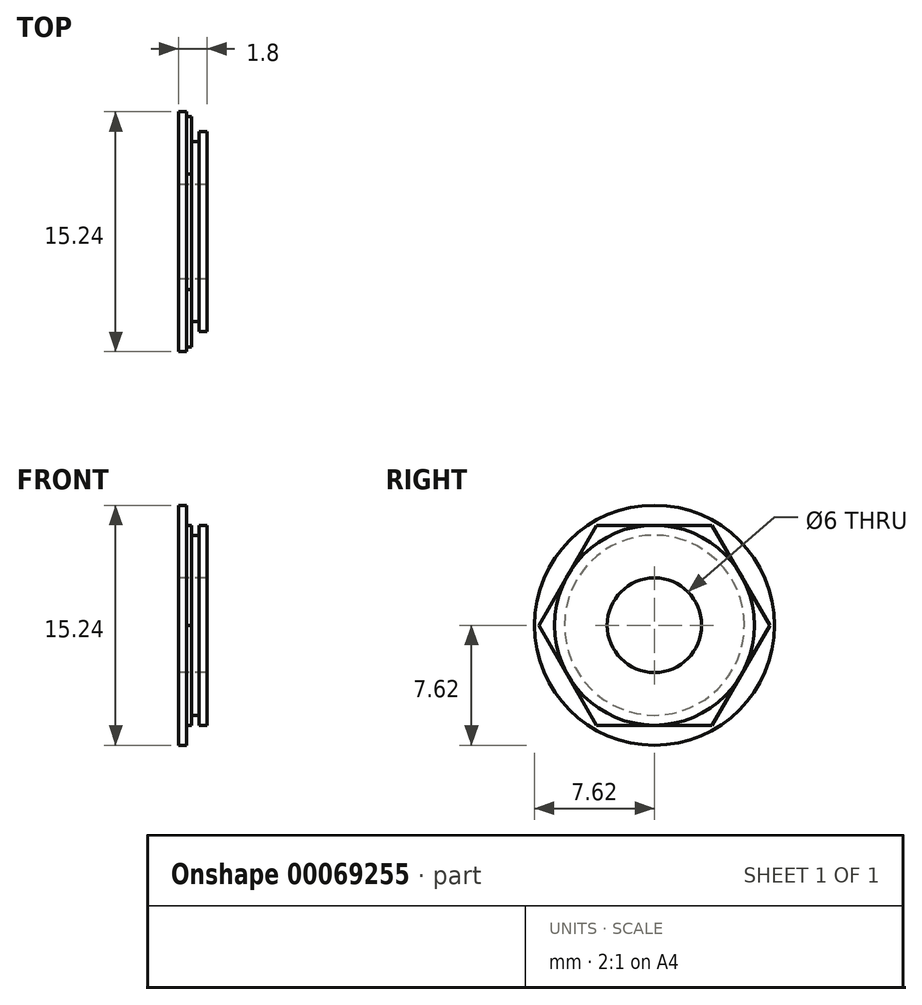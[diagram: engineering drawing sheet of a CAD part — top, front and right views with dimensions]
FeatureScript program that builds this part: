
annotation { "Feature Type Name" : "Feature", "Feature Type Description" : "" }
export const myFeature = defineFeature(function(context is Context, id is Id, definition is map)
    precondition{}
    {
        {
            assignVariable(context, id + "F0", {"name" : "shoulder_length", "anyValue" : .5});
        }
        {
            assignVariable(context, id + "F1", {"name" : "hex_length", "anyValue" : 0.3});
        }
        {
            var Q0;
            Q0=qCreatedBy(makeId("Right.planeOp"),FACE);
            var sketch = newSketch(context, id + "F2", { "sketchPlane" : qUnion([Q0])});
            skCircle(sketch, "E0", {"center": v(0, 0) * mm, "radius": 7.62 * mm});
            skCircle(sketch, "E1.cCircle", {"center": v(0, 0) * mm, "radius": 6.35 * mm});
            skLineSegment(sketch, "E1.0", {"start": v(-3.67, 6.35) * mm, "end": v(3.67, 6.35) * mm});
            skLineSegment(sketch, "E1.1", {"start": v(3.67, 6.35) * mm, "end": v(7.33, 0) * mm});
            skLineSegment(sketch, "E1.2", {"start": v(7.33, 0) * mm, "end": v(3.67, -6.35) * mm});
            skLineSegment(sketch, "E1.3", {"start": v(3.67, -6.35) * mm, "end": v(-3.67, -6.35) * mm});
            skLineSegment(sketch, "E1.4", {"start": v(-3.67, -6.35) * mm, "end": v(-7.33, 0) * mm});
            skLineSegment(sketch, "E1.5", {"start": v(-7.33, 0) * mm, "end": v(-3.67, 6.35) * mm});
            skPoint(sketch, "E1.0.midPoint", {"position": v(0, 6.35) * mm});
            skCircle(sketch, "E2.0", {"center": v(0, 0) * mm, "radius": 5.72 * mm});
            skCircle(sketch, "E3", {"center": v(0, 0) * mm, "radius": 3 * mm});
            skSolve(sketch);
        }
        {
            var Q0;
            Q0=makeQuery(id+"F2.imprint","IMPRINT",FACE,{"disambiguationData":[TD([[makeQuery(id+"F2.imprint","IMPRINT",EDGE,{"derivedFrom":sQuery(id+"F2.wireOp",EDGE,"E0")}),1.0]])]});
            extrude(context, id + "F3", {"entities" : qUnion([Q0]), "depth" : (getVariable(context, 'shoulder_length')) * mm});
        }
        {
            var Q0;
            {var subQ0=sQuery(id+"F2.wireOp",EDGE,"E1.0");var subQ1=sQuery(id+"F2.wireOp",EDGE,"E1.cCircle");var subQ2=makeQuery(id+"F2.imprint","INTERSECT",VERTEX,{"derivedFrom":[subQ1,subQ0]});Q0=makeQuery(id+"F2.imprint","IMPRINT",FACE,{"disambiguationData":[TD([[makeQuery(id+"F2.imprint","IMPRINT",EDGE,{"disambiguationData":[TD([[subQ2,-1.0]])],"derivedFrom":subQ1}),-1.0]])]});}
            var Q1;
            {var subQ0=sQuery(id+"F2.wireOp",EDGE,"E1.0");var subQ1=sQuery(id+"F2.wireOp",EDGE,"E1.cCircle");var subQ2=makeQuery(id+"F2.imprint","INTERSECT",VERTEX,{"derivedFrom":[subQ1,subQ0]});Q1=makeQuery(id+"F2.imprint","IMPRINT",FACE,{"disambiguationData":[TD([[makeQuery(id+"F2.imprint","IMPRINT",EDGE,{"disambiguationData":[TD([[subQ2,1.0]])],"derivedFrom":subQ1}),-1.0]])]});}
            var Q2;
            {var subQ0=sQuery(id+"F2.wireOp",EDGE,"E1.1");var subQ1=sQuery(id+"F2.wireOp",EDGE,"E1.cCircle");var subQ2=makeQuery(id+"F2.imprint","INTERSECT",VERTEX,{"derivedFrom":[subQ1,subQ0]});Q2=makeQuery(id+"F2.imprint","IMPRINT",FACE,{"disambiguationData":[TD([[makeQuery(id+"F2.imprint","IMPRINT",EDGE,{"disambiguationData":[TD([[subQ2,1.0]])],"derivedFrom":subQ1}),-1.0]])]});}
            var Q3;
            {var subQ0=sQuery(id+"F2.wireOp",EDGE,"E1.3");var subQ1=sQuery(id+"F2.wireOp",EDGE,"E1.cCircle");var subQ2=makeQuery(id+"F2.imprint","INTERSECT",VERTEX,{"derivedFrom":[subQ1,subQ0]});Q3=makeQuery(id+"F2.imprint","IMPRINT",FACE,{"disambiguationData":[TD([[makeQuery(id+"F2.imprint","IMPRINT",EDGE,{"disambiguationData":[TD([[subQ2,-1.0]])],"derivedFrom":subQ1}),-1.0]])]});}
            var Q4;
            {var subQ0=sQuery(id+"F2.wireOp",EDGE,"E1.4");var subQ1=sQuery(id+"F2.wireOp",EDGE,"E1.cCircle");var subQ2=makeQuery(id+"F2.imprint","INTERSECT",VERTEX,{"derivedFrom":[subQ1,subQ0]});Q4=makeQuery(id+"F2.imprint","IMPRINT",FACE,{"disambiguationData":[TD([[makeQuery(id+"F2.imprint","IMPRINT",EDGE,{"disambiguationData":[TD([[subQ2,-1.0]])],"derivedFrom":subQ1}),-1.0]])]});}
            var Q5;
            {var subQ0=sQuery(id+"F2.wireOp",EDGE,"E1.5");var subQ1=sQuery(id+"F2.wireOp",EDGE,"E1.cCircle");var subQ2=makeQuery(id+"F2.imprint","INTERSECT",VERTEX,{"derivedFrom":[subQ1,subQ0]});Q5=makeQuery(id+"F2.imprint","IMPRINT",FACE,{"disambiguationData":[TD([[makeQuery(id+"F2.imprint","IMPRINT",EDGE,{"disambiguationData":[TD([[subQ2,-1.0]])],"derivedFrom":subQ1}),-1.0]])]});}
            var Q6;
            Q6=makeQuery(id+"F2.imprint","IMPRINT",FACE,{"disambiguationData":[TD([[makeQuery(id+"F2.imprint","IMPRINT",EDGE,{"derivedFrom":sQuery(id+"F2.wireOp",EDGE,"E2.0")}),-1.0]])]});
            extrude(context, id + "F4", {"entities" : qUnion([Q0, Q1, Q2, Q3, Q4, Q5, Q6]), "operationType" : NewBodyOperationType.ADD, "depth" : (getVariable(context, 'shoulder_length') + getVariable(context, 'hex_length')) * mm});
        }
        {
            var Q0;
            Q0=makeQuery(id+"F2.imprint","IMPRINT",FACE,{"disambiguationData":[TD([[makeQuery(id+"F2.imprint","IMPRINT",EDGE,{"derivedFrom":sQuery(id+"F2.wireOp",EDGE,"E2.0")}),1.0]])]});
            extrude(context, id + "F5", {"entities" : qUnion([Q0]), "operationType" : NewBodyOperationType.ADD, "depth" : (getVariable(context, 'hex_length') + 3 * getVariable(context, 'shoulder_length')) * mm});
        }
        {
            var Q0;
            Q0=makeQuery(id+"F2.imprint","IMPRINT",FACE,{"disambiguationData":[TD([[makeQuery(id+"F2.imprint","IMPRINT",EDGE,{"derivedFrom":sQuery(id+"F2.wireOp",EDGE,"E2.0")}),-1.0]])]});
            var Q1;
            Q1=makeQuery(id+"F5.opExtrude","CAP_FACE",FACE,{"disambiguationData":[OSD([sQuery(id+"F2.wireOp",EDGE,"E2.0")])],"isStart":false});
            extrude(context, id + "F6", {"entities" : qUnion([Q0]), "operationType" : NewBodyOperationType.ADD, "endBound" : BoundingType.UP_TO_SURFACE, "endBoundEntityFace" : qUnion([Q1]), "depth" : 25.4 * mm, "hasSecondDirection" : true, "secondDirectionOppositeDirection" : false, "secondDirectionDepth" : (getVariable(context, 'shoulder_length') * 2 + getVariable(context, 'hex_length')) * mm});
        }
        {
            var Q0;
            Q0=qCreatedBy(makeId("Top.planeOp"),FACE);
            var sketch = newSketch(context, id + "F7", { "sketchPlane" : qUnion([Q0])});
            skLineSegment(sketch, "E4.0", {"start": v(11.43, 6.35) * mm, "end": v(11.43, -6.35) * mm, "construction": true});
            skLineSegment(sketch, "E5", {"start": v(0, 0) * mm, "end": v(11.43, 0) * mm, "construction": true});
            skCircle(sketch, "E6", {"center": v(5.08, 0) * mm, "radius": 1.27 * mm});
            skLineSegment(sketch, "E7.direction1", {"start": v(5.08, 0) * mm, "end": v(15.24, 0) * mm, "construction": true});
            skCircle(sketch, "E8.0.1.0", {"center": v(15.24, 0) * mm, "radius": 1.27 * mm});
            skSolve(sketch);
        }
        {
            var Q0;
            Q0 = qSketchRegion(id + "F7", true);
            extrude(context, id + "F8", {"entities" : qUnion([Q0]), "operationType" : NewBodyOperationType.REMOVE, "endBound" : BoundingType.THROUGH_ALL, "depth" : 25.4 * mm});
        }
    });
